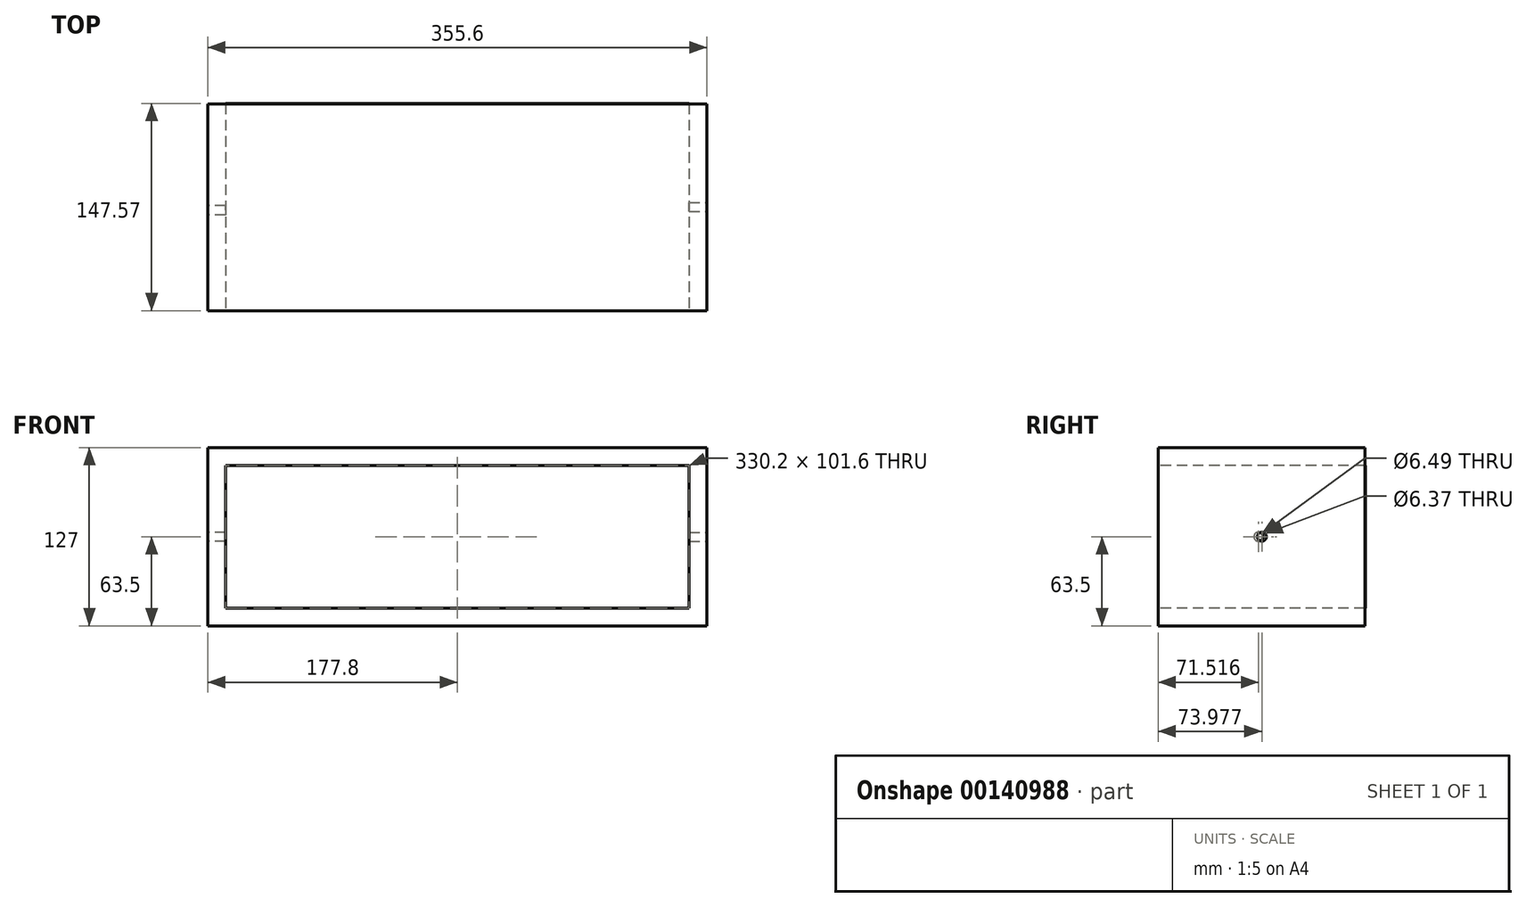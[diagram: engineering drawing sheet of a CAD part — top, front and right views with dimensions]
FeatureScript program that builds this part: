
annotation { "Feature Type Name" : "Feature", "Feature Type Description" : "" }
export const myFeature = defineFeature(function(context is Context, id is Id, definition is map)
    precondition{}
    {
        {
            var Q0;
            Q0=qCreatedBy(makeId("Front.planeOp"),FACE);
            var sketch = newSketch(context, id + "F0", { "sketchPlane" : qUnion([Q0])});
            skLineSegment(sketch, "E0.bottom", {"start": v(177.8, -63.5) * mm, "end": v(-177.8, -63.5) * mm});
            skLineSegment(sketch, "E0.top", {"start": v(177.8, 63.5) * mm, "end": v(-177.8, 63.5) * mm});
            skLineSegment(sketch, "E0.left", {"start": v(177.8, -63.5) * mm, "end": v(177.8, 63.5) * mm});
            skLineSegment(sketch, "E0.right", {"start": v(-177.8, -63.5) * mm, "end": v(-177.8, 63.5) * mm});
            skPoint(sketch, "E0.middle", {"position": v(0, 0) * mm});
            skSolve(sketch);
        }
        {
            var Q0;
            Q0=qSketchRegion(id+"F0",true);
            extrude(context, id + "F1", {"entities" : qUnion([Q0]), "depth" : 147.32 * mm});
        }
        {
            var Q0;
            Q0=makeQuery(id+"F1.opExtrude","CAP_FACE",FACE,{"disambiguationData":[OSD([sQuery(id+"F0.wireOp",EDGE,"E0.bottom"),sQuery(id+"F0.wireOp",EDGE,"E0.top"),sQuery(id+"F0.wireOp",EDGE,"E0.left"),sQuery(id+"F0.wireOp",EDGE,"E0.right")])],"isStart":false});
            var sketch = newSketch(context, id + "F2", { "sketchPlane" : qUnion([Q0])});
            skLineSegment(sketch, "E1.bottom", {"start": v(165.1, -50.8) * mm, "end": v(-165.1, -50.8) * mm});
            skLineSegment(sketch, "E1.top", {"start": v(165.1, 50.8) * mm, "end": v(-165.1, 50.8) * mm});
            skLineSegment(sketch, "E1.left", {"start": v(165.1, -50.8) * mm, "end": v(165.1, 50.8) * mm});
            skLineSegment(sketch, "E1.right", {"start": v(-165.1, -50.8) * mm, "end": v(-165.1, 50.8) * mm});
            skPoint(sketch, "E1.middle", {"position": v(0, 0) * mm});
            skSolve(sketch);
        }
        {
            var Q0;
            Q0=qSketchRegion(id+"F2",true);
            extrude(context, id + "F3", {"entities" : qUnion([Q0]), "operationType" : NewBodyOperationType.REMOVE, "endBound" : BoundingType.UP_TO_NEXT, "oppositeDirection" : true, "depth" : 25.4 * mm});
        }
        {
            var Q0;
            Q0=makeQuery(id+"F1.opExtrude","CAP_FACE",FACE,{"disambiguationData":[OSD([sQuery(id+"F0.wireOp",EDGE,"E0.bottom"),sQuery(id+"F0.wireOp",EDGE,"E0.top"),sQuery(id+"F0.wireOp",EDGE,"E0.left"),sQuery(id+"F0.wireOp",EDGE,"E0.right")])],"isStart":true});
            var sketch = newSketch(context, id + "F4", { "sketchPlane" : qUnion([Q0])});
            skLineSegment(sketch, "E2.bottom", {"start": v(-165.1, 50.8) * mm, "end": v(165.1, 50.8) * mm});
            skLineSegment(sketch, "E2.top", {"start": v(-165.1, -50.8) * mm, "end": v(165.1, -50.8) * mm});
            skLineSegment(sketch, "E2.left", {"start": v(-165.1, 50.8) * mm, "end": v(-165.1, -50.8) * mm});
            skLineSegment(sketch, "E2.right", {"start": v(165.1, 50.8) * mm, "end": v(165.1, -50.8) * mm});
            skSolve(sketch);
        }
        {
            var Q0;
            Q0=makeQuery(id+"F4.imprint","IMPRINT",FACE,{"disambiguationData":[TD([[makeQuery(id+"F4.imprint","IMPRINT",EDGE,{"derivedFrom":sQuery(id+"F4.wireOp",EDGE,"E2.bottom")}),1.0]])]});
            extrude(context, id + "F5", {"entities" : qUnion([Q0]), "depth" : 0.25 * mm});
        }
        {
            var Q0;
            Q0=makeQuery(id+"F1.opExtrude","SWEPT_FACE",FACE,{"disambiguationData":[OSD([sQuery(id+"F0.wireOp",EDGE,"E0.right")])]});
            var sketch = newSketch(context, id + "F6", { "sketchPlane" : qUnion([Q0])});
            skCircle(sketch, "E3", {"center": v(75.8, 0) * mm, "radius": 3.25 * mm});
            skSolve(sketch);
        }
        {
            var Q0;
            Q0=qSketchRegion(id+"F6",true);
            extrude(context, id + "F7", {"entities" : qUnion([Q0]), "operationType" : NewBodyOperationType.REMOVE, "oppositeDirection" : true, "depth" : 25.4 * mm});
        }
        {
            var Q0;
            Q0=makeQuery(id+"F1.opExtrude","SWEPT_FACE",FACE,{"disambiguationData":[OSD([sQuery(id+"F0.wireOp",EDGE,"E0.left")])]});
            var sketch = newSketch(context, id + "F8", { "sketchPlane" : qUnion([Q0])});
            skCircle(sketch, "E4", {"center": v(-73.34, 0) * mm, "radius": 3.19 * mm});
            skSolve(sketch);
        }
        {
            var Q0;
            Q0=qSketchRegion(id+"F8",true);
            extrude(context, id + "F9", {"entities" : qUnion([Q0]), "operationType" : NewBodyOperationType.REMOVE, "oppositeDirection" : true, "depth" : 25.4 * mm});
        }
    });
